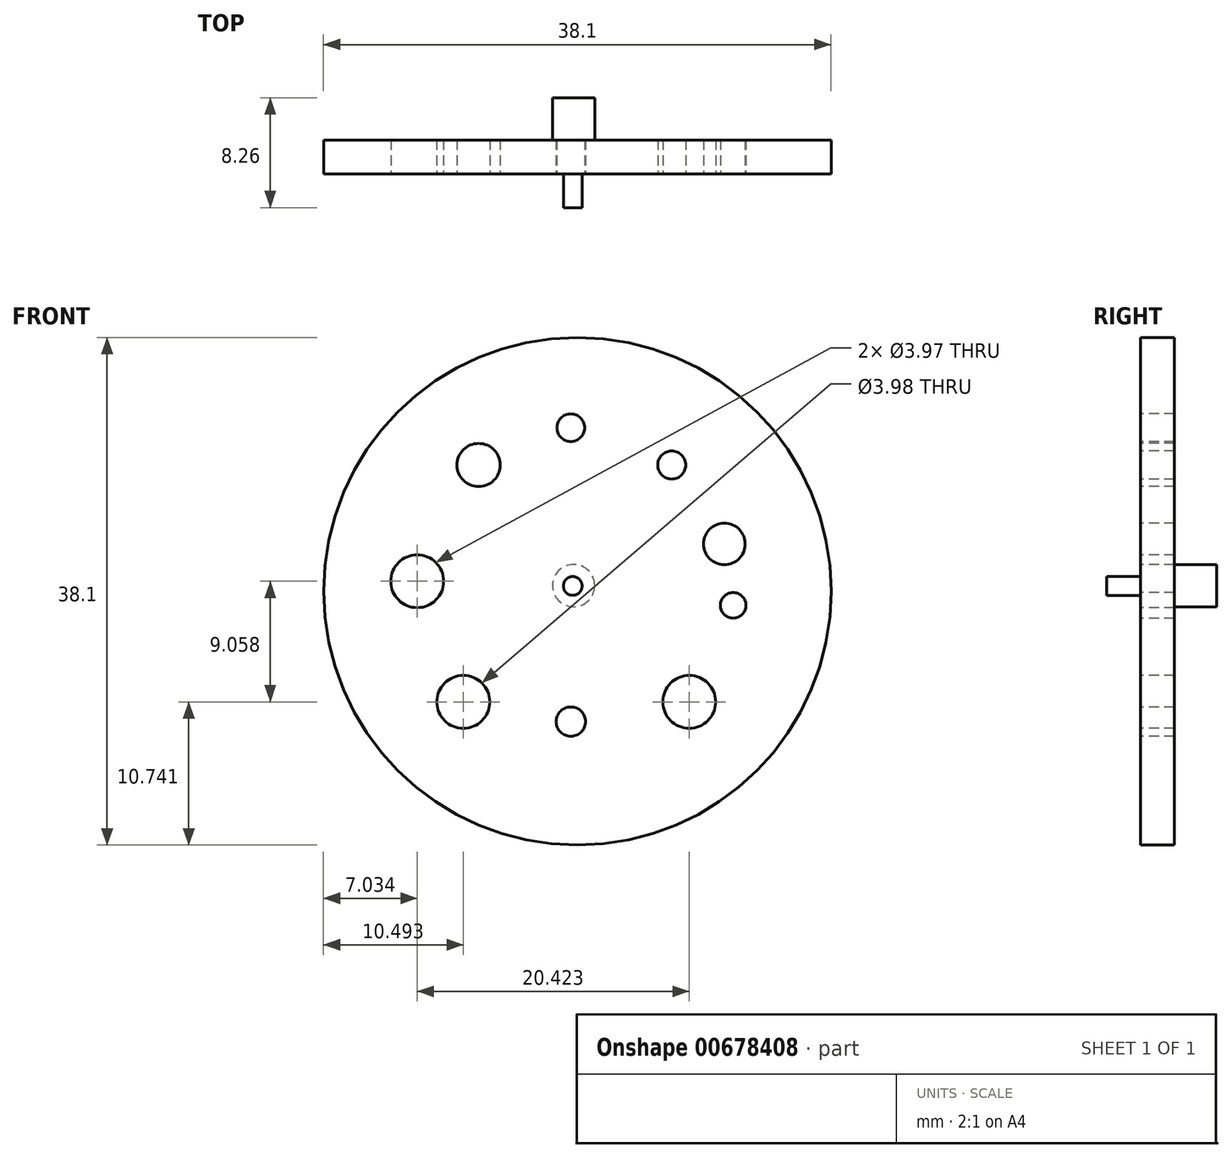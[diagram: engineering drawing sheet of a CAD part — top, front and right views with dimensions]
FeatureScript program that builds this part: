
annotation { "Feature Type Name" : "Feature", "Feature Type Description" : "" }
export const myFeature = defineFeature(function(context is Context, id is Id, definition is map)
    precondition{}
    {
        {
            var Q0;
            Q0=qCreatedBy(makeId("Front.planeOp"),FACE);
            var sketch = newSketch(context, id + "F0", { "sketchPlane" : qUnion([Q0])});
            skCircle(sketch, "E0", {"center": v(-40.39, 44.07) * mm, "radius": 19.05 * mm});
            skSolve(sketch);
        }
        {
            var Q0;
            Q0=makeQuery(id+"F0.imprint","IMPRINT",FACE,{"disambiguationData":[TD([[makeQuery(id+"F0.imprint","IMPRINT",EDGE,{"derivedFrom":sQuery(id+"F0.wireOp",EDGE,"E0")}),1.0]])]});
            extrude(context, id + "F1", {"entities" : qUnion([Q0]), "oppositeDirection" : true, "depth" : 2.54 * mm, "offsetDistance" : 25.4 * mm});
        }
        {
            var Q0;
            Q0=makeQuery(id+"F1.opExtrude","CAP_FACE",FACE,{"disambiguationData":[OSD([sQuery(id+"F0.wireOp",EDGE,"E0")])],"isStart":true});
            var sketch = newSketch(context, id + "F2", { "sketchPlane" : qUnion([Q0])});
            skCircle(sketch, "E1", {"center": v(-40.39, 44.07) * mm, "radius": 17.58 * mm});
            skSolve(sketch);
        }
        {
            var Q0;
            Q0=makeQuery(id+"F2.imprint","IMPRINT",FACE,{"disambiguationData":[TD([[makeQuery(id+"F2.imprint","IMPRINT",EDGE,{"derivedFrom":sQuery(id+"F2.wireOp",EDGE,"E1")}),1.0]])]});
            var sketch = newSketch(context, id + "F3", { "sketchPlane" : qUnion([Q0])});
            skCircle(sketch, "E2", {"center": v(-40.88, 56.35) * mm, "radius": 1.04 * mm});
            skCircle(sketch, "E3", {"center": v(-33.3, 53.55) * mm, "radius": 1.05 * mm});
            skCircle(sketch, "E4", {"center": v(-29.35, 47.62) * mm, "radius": 1.56 * mm});
            skCircle(sketch, "E5", {"center": v(-28.69, 43) * mm, "radius": 0.96 * mm});
            skCircle(sketch, "E6", {"center": v(-31.98, 35.76) * mm, "radius": 1.98 * mm});
            skCircle(sketch, "E7", {"center": v(-40.88, 34.28) * mm, "radius": 1.1 * mm});
            skCircle(sketch, "E8", {"center": v(-48.95, 35.76) * mm, "radius": 2 * mm});
            skCircle(sketch, "E9", {"center": v(-52.4, 44.82) * mm, "radius": 1.98 * mm});
            skCircle(sketch, "E10", {"center": v(-47.8, 53.55) * mm, "radius": 1.62 * mm});
            skSolve(sketch);
        }
        {
            var Q0;
            Q0 = qSketchRegion(id + "F3", true);
            extrude(context, id + "F4", {"entities" : qUnion([Q0]), "operationType" : NewBodyOperationType.REMOVE, "oppositeDirection" : true, "depth" : 25.4 * mm, "offsetDistance" : 25.4 * mm});
        }
        {
            var Q0;
            Q0=makeQuery(id+"F2.imprint","IMPRINT",FACE,{"disambiguationData":[TD([[makeQuery(id+"F2.imprint","IMPRINT",EDGE,{"derivedFrom":sQuery(id+"F2.wireOp",EDGE,"E1")}),1.0]])]});
            var sketch = newSketch(context, id + "F5", { "sketchPlane" : qUnion([Q0])});
            skCircle(sketch, "E11", {"center": v(-40.72, 44.43) * mm, "radius": 1.58 * mm});
            skSolve(sketch);
        }
        {
            var Q0;
            Q0=makeQuery(id+"F5.imprint","IMPRINT",FACE,{"disambiguationData":[TD([[makeQuery(id+"F5.imprint","IMPRINT",EDGE,{"derivedFrom":sQuery(id+"F5.wireOp",EDGE,"E11")}),-1.0]])]});
            var sketch = newSketch(context, id + "F6", { "sketchPlane" : qUnion([Q0])});
            skCircle(sketch, "E12", {"center": v(-40.73, 44.47) * mm, "radius": 0.7 * mm});
            skSolve(sketch);
        }
        {
            var Q0;
            Q0 = qSketchRegion(id + "F6", true);
            extrude(context, id + "F7", {"entities" : qUnion([Q0]), "operationType" : NewBodyOperationType.ADD, "depth" : 2.54 * mm, "offsetDistance" : 25.4 * mm});
        }
        {
            var Q0;
            Q0=makeQuery(id+"F1.opExtrude","CAP_FACE",FACE,{"disambiguationData":[OSD([sQuery(id+"F0.wireOp",EDGE,"E0")])],"isStart":false});
            var sketch = newSketch(context, id + "F8", { "sketchPlane" : qUnion([Q0])});
            skCircle(sketch, "E13", {"center": v(40.67, 44.5) * mm, "radius": 1.59 * mm});
            skSolve(sketch);
        }
        {
            var Q0;
            Q0=makeQuery(id+"F8.imprint","IMPRINT",FACE,{"disambiguationData":[TD([[makeQuery(id+"F8.imprint","IMPRINT",EDGE,{"derivedFrom":sQuery(id+"F8.wireOp",EDGE,"E13")}),1.0]])]});
            extrude(context, id + "F9", {"entities" : qUnion([Q0]), "operationType" : NewBodyOperationType.ADD, "depth" : 3.17 * mm, "offsetDistance" : 25.4 * mm});
        }
    });
